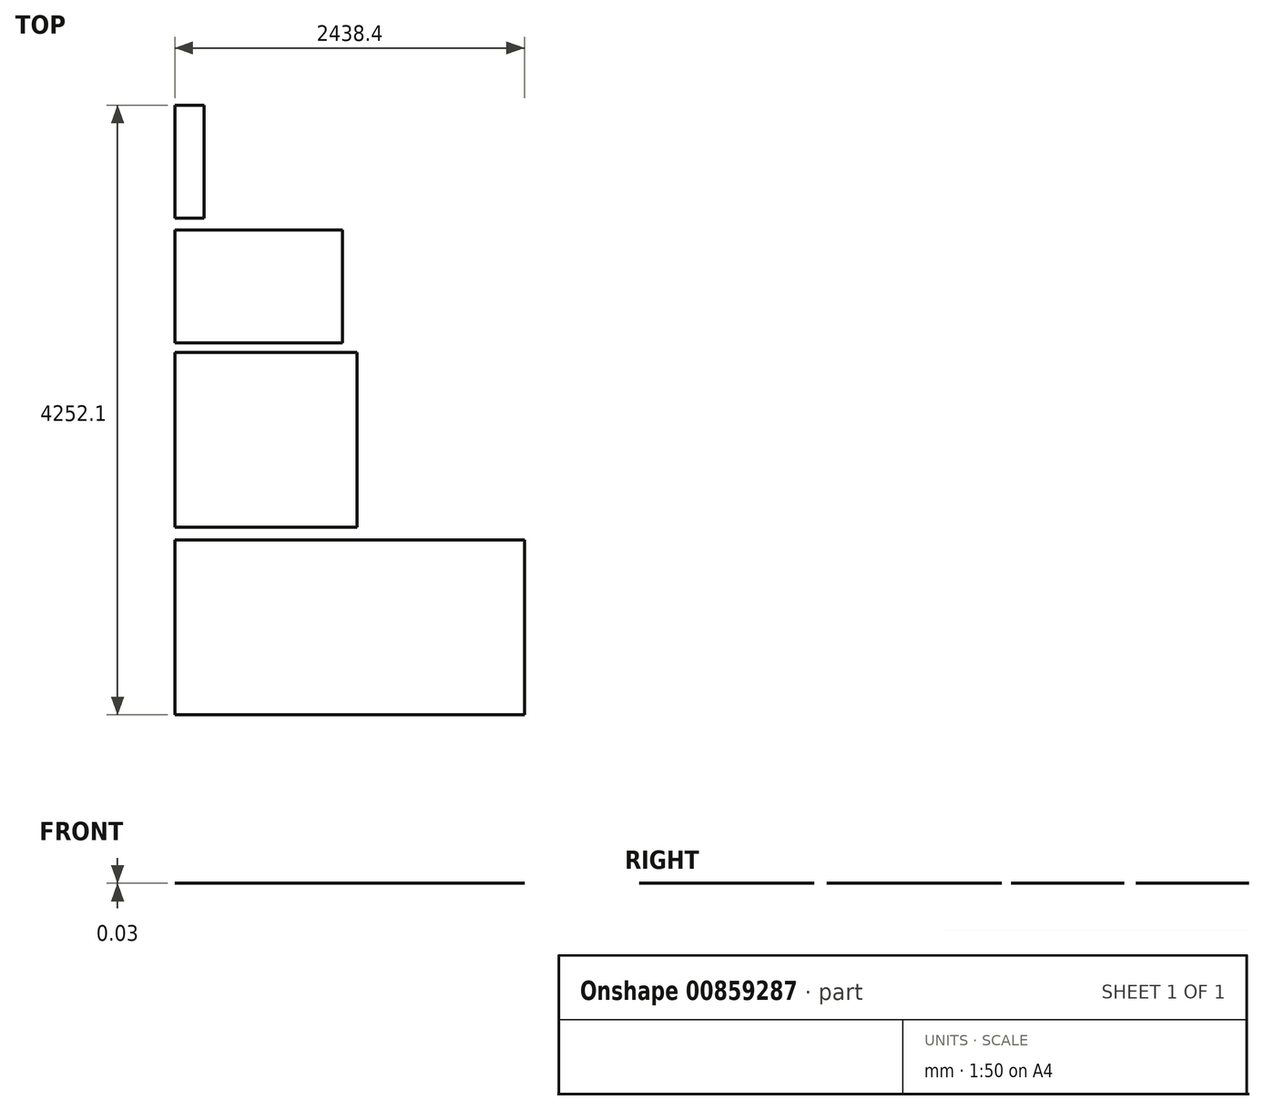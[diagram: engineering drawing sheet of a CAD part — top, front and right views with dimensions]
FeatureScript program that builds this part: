
annotation { "Feature Type Name" : "Feature", "Feature Type Description" : "" }
export const myFeature = defineFeature(function(context is Context, id is Id, definition is map)
    precondition{}
    {
        {
            var Q0;
            Q0=qCreatedBy(makeId("Top.planeOp"),FACE);
            var sketch = newSketch(context, id + "F0", { "sketchPlane" : qUnion([Q0])});
            skLineSegment(sketch, "E0.bottom", {"start": v(0, 0) * mm, "end": v(2438.4, 0) * mm});
            skLineSegment(sketch, "E0.top", {"start": v(0, 1219.2) * mm, "end": v(2438.4, 1219.2) * mm});
            skLineSegment(sketch, "E0.left", {"start": v(0, 0) * mm, "end": v(0, 1219.2) * mm});
            skLineSegment(sketch, "E0.right", {"start": v(2438.4, 0) * mm, "end": v(2438.4, 1219.2) * mm});
            skLineSegment(sketch, "E1.bottom", {"start": v(0, 1308.57) * mm, "end": v(1270, 1308.57) * mm});
            skLineSegment(sketch, "E1.top", {"start": v(0, 2527.77) * mm, "end": v(1270, 2527.77) * mm});
            skLineSegment(sketch, "E1.left", {"start": v(0, 1308.57) * mm, "end": v(0, 2527.77) * mm});
            skLineSegment(sketch, "E1.right", {"start": v(1270, 1308.57) * mm, "end": v(1270, 2527.77) * mm});
            skLineSegment(sketch, "E2.bottom", {"start": v(0, 2595.1) * mm, "end": v(1168.4, 2595.1) * mm});
            skLineSegment(sketch, "E2.top", {"start": v(0, 3382.5) * mm, "end": v(1168.4, 3382.5) * mm});
            skLineSegment(sketch, "E2.left", {"start": v(0, 2595.1) * mm, "end": v(0, 3382.5) * mm});
            skLineSegment(sketch, "E2.right", {"start": v(1168.4, 2595.1) * mm, "end": v(1168.4, 3382.5) * mm});
            skLineSegment(sketch, "E3.bottom", {"start": v(0, 3464.7) * mm, "end": v(203.2, 3464.7) * mm});
            skLineSegment(sketch, "E3.top", {"start": v(0, 4252.1) * mm, "end": v(203.2, 4252.1) * mm});
            skLineSegment(sketch, "E3.left", {"start": v(0, 3464.7) * mm, "end": v(0, 4252.1) * mm});
            skLineSegment(sketch, "E3.right", {"start": v(203.2, 3464.7) * mm, "end": v(203.2, 4252.1) * mm});
            skSolve(sketch);
        }
        {
            var Q0;
            Q0=makeQuery(id+"F0.imprint","IMPRINT",FACE,{"disambiguationData":[TD([[makeQuery(id+"F0.imprint","IMPRINT",EDGE,{"derivedFrom":sQuery(id+"F0.wireOp",EDGE,"E0.bottom")}),1.0]])]});
            var Q1;
            Q1=makeQuery(id+"F0.imprint","IMPRINT",FACE,{"disambiguationData":[TD([[makeQuery(id+"F0.imprint","IMPRINT",EDGE,{"derivedFrom":sQuery(id+"F0.wireOp",EDGE,"E1.bottom")}),1.0]])]});
            var Q2;
            Q2=makeQuery(id+"F0.imprint","IMPRINT",FACE,{"disambiguationData":[TD([[makeQuery(id+"F0.imprint","IMPRINT",EDGE,{"derivedFrom":sQuery(id+"F0.wireOp",EDGE,"E2.bottom")}),1.0]])]});
            var Q3;
            Q3=makeQuery(id+"F0.imprint","IMPRINT",FACE,{"disambiguationData":[TD([[makeQuery(id+"F0.imprint","IMPRINT",EDGE,{"derivedFrom":sQuery(id+"F0.wireOp",EDGE,"E3.bottom")}),1.0]])]});
            extrude(context, id + "F1", {"entities" : qUnion([Q0, Q1, Q2, Q3]), "depth" : 3 / 101.6 * mm, "offsetDistance" : 25.4 * mm});
        }
    });
